# Revit family: Shower-Showerhead-KOHLER-Fairfax-K-45412
name_source: partatom
category: Plumbing Fixtures
revit_build: Autodesk Revit 2015 (Build: 20140606_1530(x64)
units: mm (PartAtom-declared; Revit-internal decimal feet)

## types (6) — shared parameters
ADA Compliant = No
Assembly Code = D2010700
CW Connection = No
Cold Water Inlet = Cold Water Inlet
Date Modified = 12/12/2018
Default Elevation = 0"
Drain Included = No
Flow Rate = 2 GPM
HW Connection = Yes
Height = 5 1/2"
Hot Water Inlet = Tempered Water Inlet
Length = 4"
Manufacturer = KOHLER Co.
MasterFormat 1995 = 15410
MasterFormat 2004 = 22.41.23
Material = Premium Metal Construction
Panel Thickness = 0"
Pressure = 80.00 psi
Product Documentation Link = http://www.us.kohler.com
Product Name = Fairfax
Product Page URL = http://www.us.kohler.com
URL = https://www.us.kohler.com
Vent Connection = No
Waste Connection = No
Waste Water Outlet = Waste Water Outlet
Width = 5 1/2"

## per-type parameters (varying)
| type | 1.75GPM | 2GPM | Description | Finish | Model | Type |
| 2GPM, CP-Polished Chrome | No | Yes | 2.0 gpm single-function showerhead with Katalyst air-induction technology | Kohler-Metal-CP-Polished_Chrome | K-45412-CP | 1 |
| 2GPM, BN-Vibrant Brushed Nickel | No | Yes | 2.0 gpm single-function showerhead with Katalyst air-induction technology | Kohler-Metal-BN-Vibrant_Brushed_Nickel | K-45412-BN | 2 |
| 2GPM, 2BZ-Oil-Rubbed Bronze | No | Yes | 2.0 gpm single-function showerhead with Katalyst air-induction technology | Kohler-Metal-2BZ-Oil_Rubbed_Bronze | K-45412-2BZ | 3 |
| 1.75GPM, CP-Polished Chrome | Yes | No | 1.75 gpm single-function showerhead with Katalyst air-induction technology | Kohler-Metal-CP-Polished_Chrome | K-45412-G-CP | 4 |
| 1.75GPM, BN-Vibrant Brushed Nickel | Yes | No | 1.75 gpm single-function showerhead with Katalyst air-induction technology | Kohler-Metal-BN-Vibrant_Brushed_Nickel | K-45412-G-BN | 5 |
| 1.75GPM, 2BZ-Oil-Rubbed Bronze | Yes | No | 1.75 gpm single-function showerhead with Katalyst air-induction technology | Kohler-Metal-2BZ-Oil_Rubbed_Bronze | K-45412-G-2BZ | 6 |

## geometry (parser evidence)
native form markers: Sweep x5
no freeform markers — native parametric forms only
